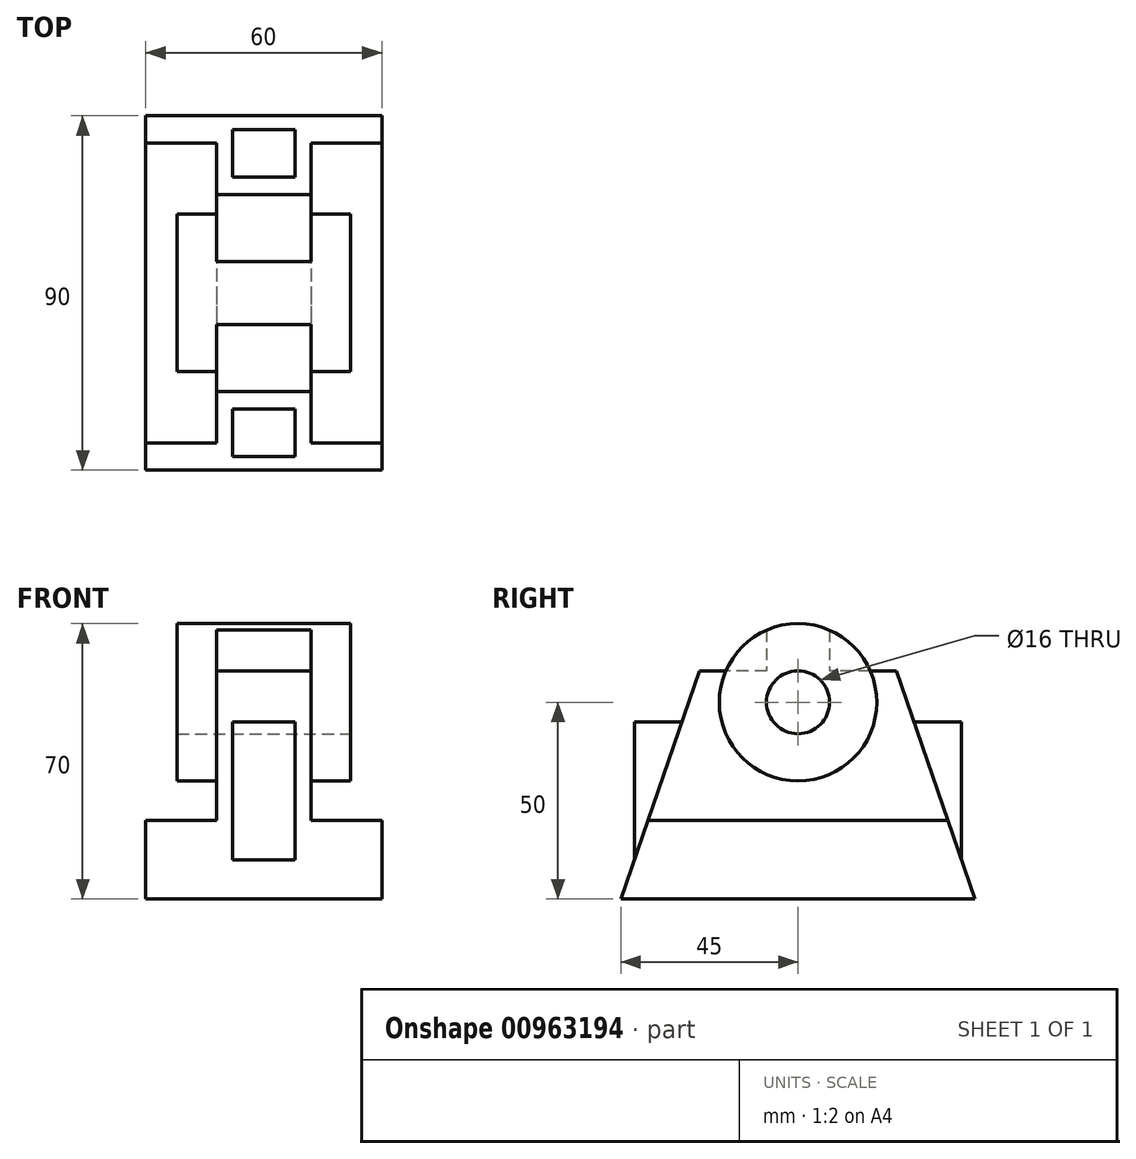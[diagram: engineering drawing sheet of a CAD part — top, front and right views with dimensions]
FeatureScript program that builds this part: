
annotation { "Feature Type Name" : "Feature", "Feature Type Description" : "" }
export const myFeature = defineFeature(function(context is Context, id is Id, definition is map)
    precondition{}
    {
        {
            var Q0;
            Q0=qCreatedBy(makeId("Right.planeOp"),FACE);
            var sketch = newSketch(context, id + "F0", { "sketchPlane" : qUnion([Q0])});
            skLineSegment(sketch, "E0", {"start": v(-45, 0) * mm, "end": v(45, 0) * mm});
            skLineSegment(sketch, "E1", {"start": v(45, 0) * mm, "end": v(25, 58) * mm});
            skLineSegment(sketch, "E2", {"start": v(25, 58) * mm, "end": v(-25, 58) * mm});
            skLineSegment(sketch, "E3", {"start": v(-25, 58) * mm, "end": v(-45, 0) * mm});
            skSolve(sketch);
        }
        {
            var Q0;
            Q0=makeQuery(id+"F0.imprint","IMPRINT",FACE,{"disambiguationData":[TD([[makeQuery(id+"F0.imprint","IMPRINT",EDGE,{"derivedFrom":sQuery(id+"F0.wireOp",EDGE,"E0")}),1.0]])]});
            extrude(context, id + "F1", {"entities" : qUnion([Q0]), "endBound" : BoundingType.SYMMETRIC, "depth" : 60 * mm, "offsetDistance" : 25 * mm});
        }
        {
            var Q0;
            Q0=makeQuery(id+"F1.opExtrude","SWEPT_FACE",FACE,{"disambiguationData":[OSD([sQuery(id+"F0.wireOp",EDGE,"E2")])]});
            var sketch = newSketch(context, id + "F2", { "sketchPlane" : qUnion([Q0])});
            skLineSegment(sketch, "E4.bottom", {"start": v(30, 45) * mm, "end": v(12, 45) * mm});
            skLineSegment(sketch, "E4.top", {"start": v(30, -45) * mm, "end": v(12, -45) * mm});
            skLineSegment(sketch, "E4.left", {"start": v(30, 45) * mm, "end": v(30, -45) * mm});
            skLineSegment(sketch, "E4.right", {"start": v(12, 45) * mm, "end": v(12, -45) * mm});
            skLineSegment(sketch, "E5.MirrorCS", {"start": v(-12, 45) * mm, "end": v(-12, -45) * mm});
            skLineSegment(sketch, "E6.MirrorCS", {"start": v(-30, 45) * mm, "end": v(-30, -45) * mm});
            skLineSegment(sketch, "E7.MirrorCS", {"start": v(-30, 45) * mm, "end": v(-12, 45) * mm});
            skLineSegment(sketch, "E8.MirrorCS", {"start": v(-30, -45) * mm, "end": v(-12, -45) * mm});
            skSolve(sketch);
        }
        {
            var Q0;
            {var subQ0=sQuery(id+"F2.wireOp",EDGE,"E4.top");Q0=makeQuery(id+"F2.imprint","IMPRINT",FACE,{"disambiguationData":[TD([[makeQuery(id+"F2.imprint","IMPRINT",EDGE,{"derivedFrom":subQ0}),-1.0]])]});}
            var Q1;
            {var subQ0=sQuery(id+"F2.wireOp",EDGE,"E4.left");var subQ1=sQuery(id+"F0.wireOp",EDGE,"E2");var subQ2=makeQuery(id+"F1.opExtrude","SWEPT_EDGE",EDGE,{"disambiguationData":[OSD([sQuery(id+"F0.wireOp",EDGE,"E1"),subQ1])]});var subQ3=makeQuery(id+"F2.imprint","INTERSECT",VERTEX,{"derivedFrom":[subQ2,subQ0]});Q1=makeQuery(id+"F2.imprint","IMPRINT",FACE,{"disambiguationData":[TD([[makeQuery(id+"F2.imprint","IMPRINT",EDGE,{"disambiguationData":[TD([[subQ3,-1.0]])],"derivedFrom":subQ0}),-1.0]])]});}
            var Q2;
            {var subQ0=sQuery(id+"F2.wireOp",EDGE,"E4.bottom");Q2=makeQuery(id+"F2.imprint","IMPRINT",FACE,{"disambiguationData":[TD([[makeQuery(id+"F2.imprint","IMPRINT",EDGE,{"derivedFrom":subQ0}),1.0]])]});}
            extrude(context, id + "F3", {"entities" : qUnion([Q0, Q1, Q2]), "operationType" : NewBodyOperationType.REMOVE, "oppositeDirection" : true, "depth" : 25 * mm, "offsetDistance" : 25 * mm});
        }
        {
            var Q0;
            Q0 = qSketchRegion(id + "F2", true);
            extrude(context, id + "F4", {"entities" : qUnion([Q0]), "operationType" : NewBodyOperationType.REMOVE, "oppositeDirection" : true, "depth" : 38 * mm, "offsetDistance" : 25 * mm});
        }
        {
            var Q0;
            Q0=qCreatedBy(makeId("Right.planeOp"),FACE);
            var sketch = newSketch(context, id + "F5", { "sketchPlane" : qUnion([Q0])});
            skLineSegment(sketch, "E9", {"start": v(-41.55, 45) * mm, "end": v(-29.48, 45) * mm});
            skLineSegment(sketch, "E10", {"start": v(-29.48, 45) * mm, "end": v(-41.55, 10) * mm});
            skLineSegment(sketch, "E11", {"start": v(-41.55, 10) * mm, "end": v(-41.55, 45) * mm});
            skLineSegment(sketch, "E12.MirrorCS", {"start": v(41.55, 45) * mm, "end": v(29.48, 45) * mm});
            skLineSegment(sketch, "E13.MirrorCS", {"start": v(41.55, 10) * mm, "end": v(41.55, 45) * mm});
            skLineSegment(sketch, "E14.MirrorCS", {"start": v(29.48, 45) * mm, "end": v(41.55, 10) * mm});
            skSolve(sketch);
        }
        {
            var Q0;
            Q0 = qSketchRegion(id + "F5", true);
            extrude(context, id + "F6", {"entities" : qUnion([Q0]), "operationType" : NewBodyOperationType.ADD, "endBound" : BoundingType.SYMMETRIC, "depth" : 16 * mm, "offsetDistance" : 25 * mm});
        }
        {
            var Q0;
            Q0 = qSketchRegion(id + "F5", true);
            extrude(context, id + "F7", {"entities" : qUnion([Q0]), "operationType" : NewBodyOperationType.ADD, "endBound" : BoundingType.SYMMETRIC, "depth" : 16 * mm, "offsetDistance" : 25 * mm});
        }
        {
            var Q0;
            {var subQ0=sQuery(id+"F2.wireOp",EDGE,"E4.right");Q0=makeQuery(id+"F4.boolean.opBoolean","MERGE",FACE,{"derivedFrom":[makeQuery(id+"F3.boolean.opBoolean","COPY",FACE,{"derivedFrom":makeQuery(id+"F3.opExtrude","SWEPT_FACE",FACE,{"disambiguationData":[OSD([subQ0])]})})],"fromTools":[makeQuery(id+"F4.opExtrude","SWEPT_FACE",FACE,{"disambiguationData":[OSD([subQ0])]})]});}
            var sketch = newSketch(context, id + "F8", { "sketchPlane" : qUnion([Q0])});
            skCircle(sketch, "E15", {"center": v(0, 50) * mm, "radius": 20 * mm});
            skPoint(sketch, "E15.centerSnap0", {"position": v(0, 58) * mm});
            skSolve(sketch);
        }
        {
            var Q0;
            {var subQ0=sQuery(id+"F8.wireOp",EDGE,"E15");var subQ1=makeQuery(id+"F3.boolean.opBoolean","COPY",EDGE,{"derivedFrom":makeQuery(id+"F3.opExtrude","CAP_EDGE",EDGE,{"disambiguationData":[OSD([sQuery(id+"F2.wireOp",EDGE,"E4.right")])],"isStart":true})});var subQ2=makeQuery(id+"F8.imprint","INTERSECT",VERTEX,{"disambiguationData":[OD(0.0)],"derivedFrom":[subQ1,subQ0]});Q0=makeQuery(id+"F8.imprint","IMPRINT",FACE,{"disambiguationData":[TD([[makeQuery(id+"F8.imprint","IMPRINT",EDGE,{"disambiguationData":[TD([[subQ2,1.0]])],"derivedFrom":subQ0}),1.0]])]});}
            var Q1;
            {var subQ0=sQuery(id+"F8.wireOp",EDGE,"E15");var subQ1=makeQuery(id+"F3.boolean.opBoolean","COPY",EDGE,{"derivedFrom":makeQuery(id+"F3.opExtrude","CAP_EDGE",EDGE,{"disambiguationData":[OSD([sQuery(id+"F2.wireOp",EDGE,"E4.right")])],"isStart":true})});var subQ2=makeQuery(id+"F8.imprint","INTERSECT",VERTEX,{"disambiguationData":[OD(0.0)],"derivedFrom":[subQ1,subQ0]});Q1=makeQuery(id+"F8.imprint","IMPRINT",FACE,{"disambiguationData":[TD([[makeQuery(id+"F8.imprint","IMPRINT",EDGE,{"disambiguationData":[TD([[subQ2,-1.0]])],"derivedFrom":subQ0}),1.0]])]});}
            extrude(context, id + "F9", {"entities" : qUnion([Q0, Q1]), "operationType" : NewBodyOperationType.ADD, "depth" : 10 * mm, "offsetDistance" : 25 * mm, "hasSecondDirection" : true, "secondDirectionOppositeDirection" : true, "secondDirectionDepth" : 34 * mm});
        }
        {
            var Q0;
            Q0=makeQuery(id+"F9.boolean.opBoolean","SPLIT",FACE,{"disambiguationData":[TD([makeQuery(id+"F1.opExtrude","SWEPT_FACE",FACE,{"disambiguationData":[OSD([sQuery(id+"F0.wireOp",EDGE,"E3")])]})])],"derivedFrom":makeQuery(id+"F1.opExtrude","SWEPT_FACE",FACE,{"disambiguationData":[OSD([sQuery(id+"F0.wireOp",EDGE,"E2")])]})});
            var sketch = newSketch(context, id + "F10", { "sketchPlane" : qUnion([Q0])});
            skLineSegment(sketch, "E16.bottom", {"start": v(-12, -25) * mm, "end": v(12, -25) * mm});
            skLineSegment(sketch, "E16.top", {"start": v(-12, -8) * mm, "end": v(12, -8) * mm});
            skLineSegment(sketch, "E16.left", {"start": v(-12, -25) * mm, "end": v(-12, -8) * mm});
            skLineSegment(sketch, "E16.right", {"start": v(12, -25) * mm, "end": v(12, -8) * mm});
            skLineSegment(sketch, "E17.MirrorCS", {"start": v(-12, 8) * mm, "end": v(12, 8) * mm});
            skLineSegment(sketch, "E18.MirrorCS", {"start": v(-12, 25) * mm, "end": v(-12, 8) * mm});
            skLineSegment(sketch, "E19.MirrorCS", {"start": v(-12, 25) * mm, "end": v(12, 25) * mm});
            skLineSegment(sketch, "E20.MirrorCS", {"start": v(12, 25) * mm, "end": v(12, 8) * mm});
            skSolve(sketch);
        }
        {
            var Q0;
            Q0 = qSketchRegion(id + "F10", true);
            extrude(context, id + "F11", {"entities" : qUnion([Q0]), "operationType" : NewBodyOperationType.REMOVE, "endBound" : BoundingType.UP_TO_NEXT, "depth" : 25 * mm, "offsetDistance" : 25 * mm});
        }
        {
            var Q0;
            Q0=makeQuery(id+"F9.opExtrude","CAP_FACE",FACE,{"disambiguationData":[OSD([sQuery(id+"F8.wireOp",EDGE,"E15")])],"isStart":false});
            var sketch = newSketch(context, id + "F12", { "sketchPlane" : qUnion([Q0])});
            skCircle(sketch, "E21", {"center": v(0, 50) * mm, "radius": 8 * mm});
            skSolve(sketch);
        }
        {
            var Q0;
            Q0 = qSketchRegion(id + "F12", true);
            extrude(context, id + "F13", {"entities" : qUnion([Q0]), "operationType" : NewBodyOperationType.REMOVE, "endBound" : BoundingType.THROUGH_ALL, "oppositeDirection" : true, "depth" : 25 * mm, "offsetDistance" : 25 * mm});
        }
    });
